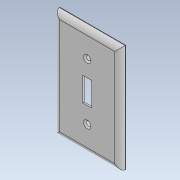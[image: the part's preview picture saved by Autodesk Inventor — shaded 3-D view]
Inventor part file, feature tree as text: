
AUTODESK INVENTOR PART (.ipt)
format: ipt  version: 2020.2 (Build 242310000, 310)  size: 131,072 bytes
history: native  units: in
note: dims shown in document units (in); Inventor stores cm internally (conversion verified against a paired STEP export)
features: extrude x3, sketch x3, fillet x2, chamfer x1
ambient origin geometry x8: Origin, YZ Plane, XZ Plane, XY Plane, X Axis, Y Axis, Z Axis, Center Point
bodies: Solid1 (feature_tree)
feature tree (9):
  extrude  "Extrusion1"  Depth=4.5in
  fillet  "Fillet1"  Radius=0.375in
  extrude  "Extrusion2"  Depth=0.2362in TaperAngle=0.0deg
  fillet  "Fillet2"  Radius=0.2165in
  extrude  "Extrusion3"  Depth=0.1575in
  chamfer  "Chamfer1"  Distance=0.1732in
  sketch  "Sketch1"  dims[d0=2.75in d1=4.5in d2=0.375in]
  sketch  "Sketch2"  dims[d3=1.0in d4=0.2362in d5=0.0in d6=0.2165in]
  sketch  "Sketch3"  dims[d9=0.1575in d10=0.1575in d11=0.1732in d12=0.0in d13=0.0787in d14=2.374in d15=0.1875in d16=1.187in d18=1.187in d19=0.0in d20=0.0in d21=0.063in d22=0.125in d23=45.0deg]
